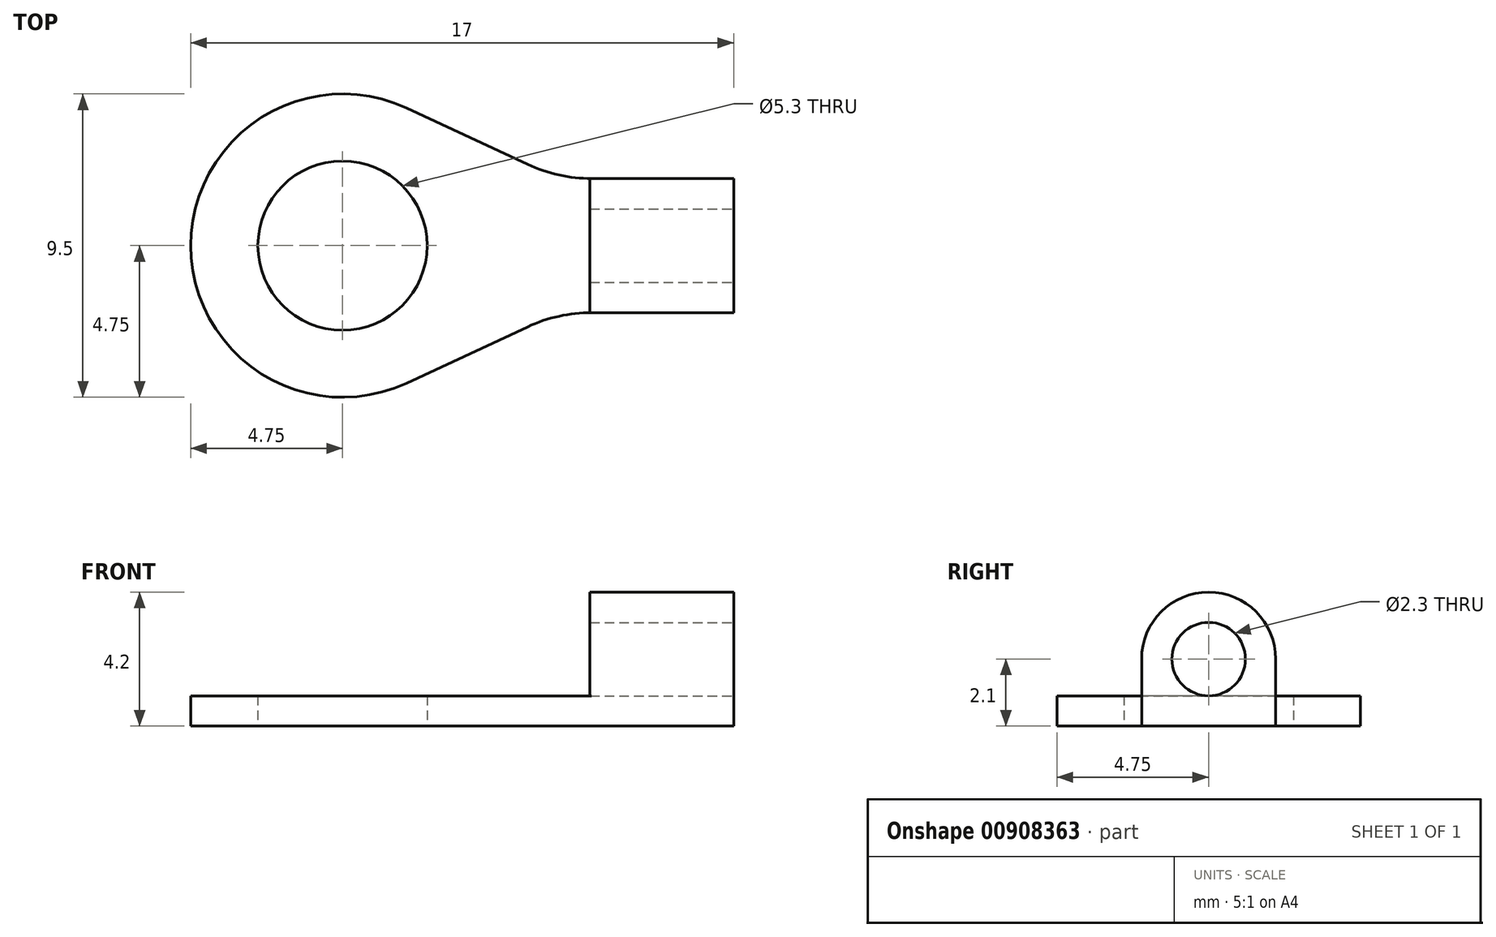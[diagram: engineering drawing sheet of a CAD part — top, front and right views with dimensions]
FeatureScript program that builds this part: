
annotation { "Feature Type Name" : "Feature", "Feature Type Description" : "" }
export const myFeature = defineFeature(function(context is Context, id is Id, definition is map)
    precondition{}
    {
        {
            var Q0;
            Q0=qCreatedBy(makeId("Top.planeOp"),FACE);
            var sketch = newSketch(context, id + "F0", { "sketchPlane" : qUnion([Q0])});
            skLineSegment(sketch, "E0.left", {"start": v(0, 4.75) * mm, "end": v(0, 4.75) * mm});
            skLineSegment(sketch, "E0.right", {"start": v(17, 2.65) * mm, "end": v(17, 6.85) * mm});
            skPoint(sketch, "E1.visualSharp", {"position": v(0, 9.5) * mm});
            skArc(sketch, "E1.filletArc", {"start": v(4.75, 9.5) * mm, "mid": v(1.4, 8.1) * mm, "end": v(0, 4.75) * mm});
            skPoint(sketch, "E2.visualSharp", {"position": v(0, 0) * mm});
            skArc(sketch, "E2.filletArc", {"start": v(0, 4.75) * mm, "mid": v(1.4, 1.4) * mm, "end": v(4.75, 0) * mm});
            skLineSegment(sketch, "E3.bottom", {"start": v(17, 2.65) * mm, "end": v(12.55, 2.65) * mm});
            skLineSegment(sketch, "E3.top", {"start": v(17, 6.85) * mm, "end": v(12.55, 6.85) * mm});
            skPoint(sketch, "E3.middle", {"position": v(17, 4.75) * mm});
            skArc(sketch, "E4", {"start": v(6.75, 9.06) * mm, "mid": v(0, 4.75) * mm, "end": v(6.75, 0.44) * mm});
            skCircle(sketch, "E5", {"center": v(4.75, 4.75) * mm, "radius": 2.65 * mm});
            skLineSegment(sketch, "E6", {"start": v(10.55, 7.3) * mm, "end": v(6.75, 9.06) * mm});
            skLineSegment(sketch, "E7", {"start": v(10.55, 2.2) * mm, "end": v(6.75, 0.44) * mm});
            skPoint(sketch, "E8.visualSharp", {"position": v(11.5, 6.85) * mm});
            skArc(sketch, "E8.filletArc", {"start": v(10.55, 7.3) * mm, "mid": v(11.52, 6.96) * mm, "end": v(12.55, 6.85) * mm});
            skPoint(sketch, "E9.visualSharp", {"position": v(11.5, 2.65) * mm});
            skArc(sketch, "E9.filletArc", {"start": v(12.55, 2.65) * mm, "mid": v(11.52, 2.54) * mm, "end": v(10.55, 2.2) * mm});
            skPoint(sketch, "E10.orphan", {"position": v(21.5, 6.85) * mm});
            skPoint(sketch, "E11.orphan", {"position": v(21.5, 2.65) * mm});
            skPoint(sketch, "E0.top.end.orphan", {"position": v(17, 9.5) * mm});
            skPoint(sketch, "E3.right.end.orphan", {"position": v(12.5, 6.85) * mm});
            skPoint(sketch, "E3.right.start.orphan", {"position": v(12.5, 2.65) * mm});
            skPoint(sketch, "E0.bottom.end.orphan", {"position": v(17, 0) * mm});
            skSolve(sketch);
        }
        {
            var Q0;
            Q0=makeQuery(id+"F0.imprint","IMPRINT",FACE,{"disambiguationData":[TD([[makeQuery(id+"F0.imprint","IMPRINT",EDGE,{"derivedFrom":sQuery(id+"F0.wireOp",EDGE,"E0.right")}),1.0]])]});
            extrude(context, id + "F1", {"entities" : qUnion([Q0]), "depth" : 0.95 * mm, "offsetDistance" : 25 * mm});
        }
        {
            var Q0;
            Q0=makeQuery(id+"F1.opExtrude","CAP_FACE",FACE,{"disambiguationData":[OSD([sQuery(id+"F0.wireOp",EDGE,"E0.right"),sQuery(id+"F0.wireOp",EDGE,"E3.bottom"),sQuery(id+"F0.wireOp",EDGE,"E3.top"),sQuery(id+"F0.wireOp",EDGE,"E4"),sQuery(id+"F0.wireOp",EDGE,"E5"),sQuery(id+"F0.wireOp",EDGE,"E6"),sQuery(id+"F0.wireOp",EDGE,"E7"),sQuery(id+"F0.wireOp",EDGE,"E8.filletArc"),sQuery(id+"F0.wireOp",EDGE,"E9.filletArc")])],"isStart":false});
            var sketch = newSketch(context, id + "F2", { "sketchPlane" : qUnion([Q0])});
            skLineSegment(sketch, "E12.bottom", {"start": v(17, 6.85) * mm, "end": v(12.5, 6.85) * mm});
            skLineSegment(sketch, "E12.top", {"start": v(17, 2.65) * mm, "end": v(12.5, 2.65) * mm});
            skLineSegment(sketch, "E12.left", {"start": v(17, 6.85) * mm, "end": v(17, 2.65) * mm});
            skLineSegment(sketch, "E12.right", {"start": v(12.5, 6.85) * mm, "end": v(12.5, 2.65) * mm});
            skSolve(sketch);
        }
        {
            var Q0;
            {var subQ0=sQuery(id+"F2.wireOp",EDGE,"E12.left");Q0=makeQuery(id+"F2.imprint","IMPRINT",FACE,{"disambiguationData":[TD([[makeQuery(id+"F2.imprint","IMPRINT",EDGE,{"derivedFrom":subQ0}),1.0]])]});}
            extrude(context, id + "F3", {"entities" : qUnion([Q0]), "operationType" : NewBodyOperationType.ADD, "depth" : 3.25 * mm, "offsetDistance" : 25 * mm});
        }
        {
            var Q0;
            Q0=makeQuery(id+"F3.opExtrude","CAP_EDGE",EDGE,{"disambiguationData":[OSD([sQuery(id+"F2.wireOp",EDGE,"E12.bottom")])],"isStart":false});
            var Q1;
            Q1=makeQuery(id+"F3.opExtrude","CAP_EDGE",EDGE,{"disambiguationData":[OSD([sQuery(id+"F2.wireOp",EDGE,"E12.top")])],"isStart":false});
            fillet(context, id + "F4", {"entities" : qUnion([Q0, Q1]), "radius" : 2.1 * mm, "tangentPropagation" : true, "allowEdgeOverflow" : false});
        }
        {
            var Q0;
            Q0=makeQuery(id+"F3.boolean.opBoolean","MERGE",FACE,{"derivedFrom":[makeQuery(id+"F1.opExtrude","SWEPT_FACE",FACE,{"disambiguationData":[OSD([sQuery(id+"F0.wireOp",EDGE,"E0.right")])]}),makeQuery(id+"F3.opExtrude","SWEPT_FACE",FACE,{"disambiguationData":[OSD([sQuery(id+"F2.wireOp",EDGE,"E12.left")])]})]});
            var sketch = newSketch(context, id + "F5", { "sketchPlane" : qUnion([Q0])});
            skCircle(sketch, "E13", {"center": v(4.75, 2.1) * mm, "radius": 1.15 * mm});
            skSolve(sketch);
        }
        {
            var Q0;
            Q0 = qSketchRegion(id + "F5", true);
            extrude(context, id + "F6", {"entities" : qUnion([Q0]), "operationType" : NewBodyOperationType.REMOVE, "oppositeDirection" : true, "depth" : 25 * mm, "offsetDistance" : 25 * mm});
        }
    });
